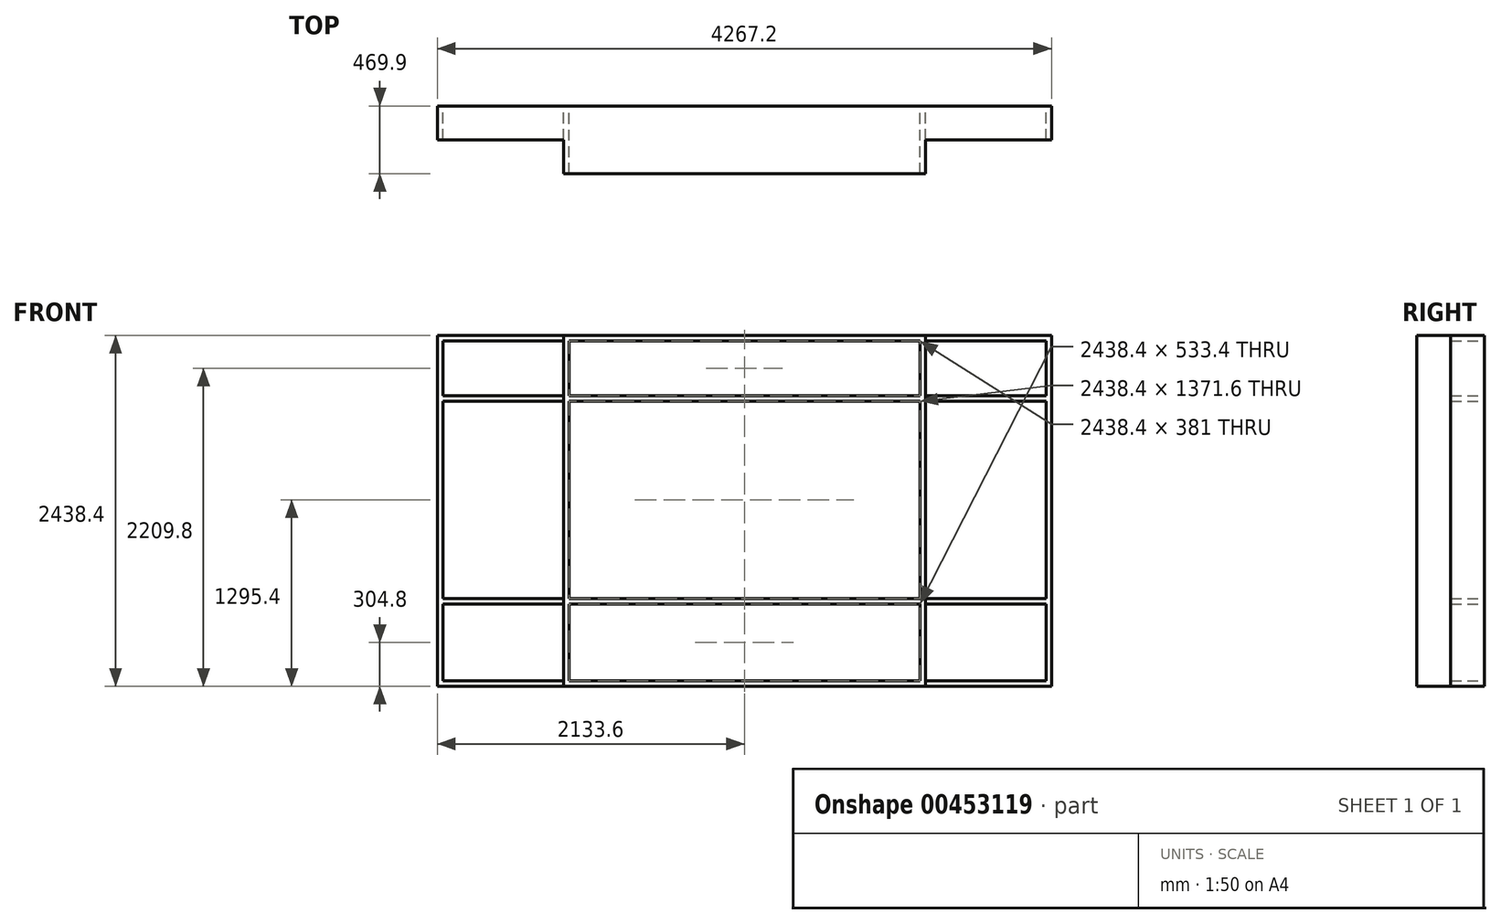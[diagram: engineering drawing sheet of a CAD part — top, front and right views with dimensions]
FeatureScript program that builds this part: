
annotation { "Feature Type Name" : "Feature", "Feature Type Description" : "" }
export const myFeature = defineFeature(function(context is Context, id is Id, definition is map)
    precondition{}
    {
        {
            var Q0;
            Q0=qCreatedBy(makeId("Front.planeOp"),FACE);
            var sketch = newSketch(context, id + "F0", { "sketchPlane" : qUnion([Q0])});
            skLineSegment(sketch, "E0.bottom", {"start": v(2133.6, 1219.2) * mm, "end": v(-2133.6, 1219.2) * mm});
            skLineSegment(sketch, "E0.top", {"start": v(2133.6, -1219.2) * mm, "end": v(457.2, -1219.2) * mm});
            skLineSegment(sketch, "E0.left", {"start": v(2133.6, 1219.2) * mm, "end": v(2133.6, -1219.2) * mm});
            skLineSegment(sketch, "E0.right", {"start": v(-2133.6, 1219.2) * mm, "end": v(-2133.6, -1219.2) * mm});
            skPoint(sketch, "E0.middle", {"position": v(0, 0) * mm});
            skLineSegment(sketch, "E1.0", {"start": v(2095.5, 762) * mm, "end": v(1257.3, 762) * mm});
            skLineSegment(sketch, "E2.0", {"start": v(-1219.2, 1181.1) * mm, "end": v(-1219.2, -1181.1) * mm});
            skLineSegment(sketch, "E3.0", {"start": v(1219.2, 1181.1) * mm, "end": v(1219.2, -1181.1) * mm});
            skLineSegment(sketch, "E4.0", {"start": v(2095.5, -609.6) * mm, "end": v(1257.3, -609.6) * mm});
            skPoint(sketch, "E5", {"position": v(-1219.2, -609.6) * mm});
            skPoint(sketch, "E6", {"position": v(1219.2, 762) * mm});
            skPoint(sketch, "E7", {"position": v(-1219.2, 762) * mm});
            skPoint(sketch, "E8", {"position": v(1219.2, -609.6) * mm});
            skLineSegment(sketch, "E9", {"start": v(457.2, -609.6) * mm, "end": v(-457.2, -609.6) * mm});
            skLineSegment(sketch, "E10", {"start": v(-457.2, -609.6) * mm, "end": v(-457.2, -609.6) * mm});
            skLineSegment(sketch, "E11", {"start": v(-457.2, -609.6) * mm, "end": v(-1219.2, -609.6) * mm});
            skLineSegment(sketch, "E12", {"start": v(-457.2, -1219.2) * mm, "end": v(-2133.6, -1219.2) * mm});
            skLineSegment(sketch, "E13", {"start": v(457.2, -1219.2) * mm, "end": v(-457.2, -1219.2) * mm});
            skLineSegment(sketch, "E14.0", {"start": v(-2095.5, 1181.1) * mm, "end": v(-2095.5, -1181.1) * mm});
            skLineSegment(sketch, "E15.0", {"start": v(-1257.3, 1181.1) * mm, "end": v(-1257.3, -1181.1) * mm});
            skLineSegment(sketch, "E16.0", {"start": v(2133.6, 1181.1) * mm, "end": v(-2133.6, 1181.1) * mm});
            skLineSegment(sketch, "E17.0", {"start": v(2095.5, 800.1) * mm, "end": v(1257.3, 800.1) * mm});
            skLineSegment(sketch, "E18.0", {"start": v(1257.3, 1181.1) * mm, "end": v(1257.3, -1181.1) * mm});
            skLineSegment(sketch, "E19.0", {"start": v(2095.5, 1181.1) * mm, "end": v(2095.5, -1181.1) * mm});
            skLineSegment(sketch, "E20.0", {"start": v(457.2, -647.7) * mm, "end": v(-457.2, -647.7) * mm});
            skLineSegment(sketch, "E21.0", {"start": v(2095.5, -647.7) * mm, "end": v(1257.3, -647.7) * mm});
            skLineSegment(sketch, "E22.0", {"start": v(-457.2, -647.7) * mm, "end": v(-1219.2, -647.7) * mm});
            skLineSegment(sketch, "E23.0", {"start": v(2133.6, -1181.1) * mm, "end": v(457.2, -1181.1) * mm});
            skLineSegment(sketch, "E24.0", {"start": v(457.2, -1181.1) * mm, "end": v(-457.2, -1181.1) * mm});
            skLineSegment(sketch, "E25.0", {"start": v(-457.2, -1181.1) * mm, "end": v(-2133.6, -1181.1) * mm});
            skLineSegment(sketch, "E26.trimOffspring", {"start": v(1219.2, -609.6) * mm, "end": v(457.2, -609.6) * mm});
            skLineSegment(sketch, "E27.trimOffspring", {"start": v(1219.2, -647.7) * mm, "end": v(457.2, -647.7) * mm});
            skLineSegment(sketch, "E28.trimOffspring", {"start": v(-1257.3, -609.6) * mm, "end": v(-2095.5, -609.6) * mm});
            skLineSegment(sketch, "E29.trimOffspring", {"start": v(-1257.3, -647.7) * mm, "end": v(-2095.5, -647.7) * mm});
            skLineSegment(sketch, "E30.trimOffspring", {"start": v(-1257.3, 800.1) * mm, "end": v(-2095.5, 800.1) * mm});
            skLineSegment(sketch, "E31.trimOffspring", {"start": v(-1257.3, 762) * mm, "end": v(-2095.5, 762) * mm});
            skLineSegment(sketch, "E32.trimOffspring", {"start": v(1219.2, 800.1) * mm, "end": v(-1219.2, 800.1) * mm});
            skLineSegment(sketch, "E33.trimOffspring", {"start": v(1219.2, 762) * mm, "end": v(-1219.2, 762) * mm});
            skLineSegment(sketch, "E34", {"start": v(1257.3, 1181.1) * mm, "end": v(1257.3, 1219.2) * mm});
            skLineSegment(sketch, "E35", {"start": v(-1257.3, 1181.1) * mm, "end": v(-1257.3, 1219.2) * mm});
            skLineSegment(sketch, "E36", {"start": v(1257.3, -1181.1) * mm, "end": v(1257.3, -1219.2) * mm});
            skLineSegment(sketch, "E37", {"start": v(-1257.3, -1181.1) * mm, "end": v(-1257.3, -1219.2) * mm});
            skSolve(sketch);
        }
        {
            var Q0;
            {var subQ3=sQuery(id+"F0.wireOp",EDGE,"E13");Q0=makeQuery(id+"F0.imprint","IMPRINT",FACE,{"disambiguationData":[TD([[makeQuery(id+"F0.imprint","IMPRINT",EDGE,{"derivedFrom":subQ3}),-1.0]])]});}
            var Q1;
            {var subQ5=sQuery(id+"F0.wireOp",EDGE,"E16.0");var subQ8=sQuery(id+"F0.wireOp",EDGE,"E3.0");var subQ11=makeQuery(id+"F0.imprint","INTERSECT",VERTEX,{"derivedFrom":[subQ8,subQ5]});Q1=makeQuery(id+"F0.imprint","IMPRINT",FACE,{"disambiguationData":[TD([[makeQuery(id+"F0.imprint","IMPRINT",EDGE,{"disambiguationData":[TD([[subQ11,-1.0]])],"derivedFrom":subQ8}),1.0]])]});}
            var Q2;
            Q2=makeQuery(id+"F0.imprint","IMPRINT",FACE,{"disambiguationData":[TD([[makeQuery(id+"F0.imprint","IMPRINT",EDGE,{"derivedFrom":sQuery(id+"F0.wireOp",EDGE,"E9")}),1.0]])]});
            var Q3;
            {var subQ0=sQuery(id+"F0.wireOp",EDGE,"E16.0");var subQ5=sQuery(id+"F0.wireOp",EDGE,"E2.0");var subQ9=makeQuery(id+"F0.imprint","INTERSECT",VERTEX,{"derivedFrom":[subQ5,subQ0]});Q3=makeQuery(id+"F0.imprint","IMPRINT",FACE,{"disambiguationData":[TD([[makeQuery(id+"F0.imprint","IMPRINT",EDGE,{"disambiguationData":[TD([[subQ9,-1.0]])],"derivedFrom":subQ5}),-1.0]])]});}
            var Q4;
            {var subQ4=sQuery(id+"F0.wireOp",EDGE,"E34");Q4=makeQuery(id+"F0.imprint","IMPRINT",FACE,{"disambiguationData":[TD([[makeQuery(id+"F0.imprint","IMPRINT",EDGE,{"derivedFrom":subQ4}),1.0]])]});}
            var Q5;
            {var subQ0=sQuery(id+"F0.wireOp",EDGE,"E32.trimOffspring");Q5=makeQuery(id+"F0.imprint","IMPRINT",FACE,{"disambiguationData":[TD([[makeQuery(id+"F0.imprint","IMPRINT",EDGE,{"derivedFrom":subQ0}),1.0]])]});}
            extrude(context, id + "F1", {"entities" : qUnion([Q0, Q1, Q2, Q3, Q4, Q5]), "depth" : 469.9 * mm});
        }
        {
            var Q0;
            {var subQ0=sQuery(id+"F0.wireOp",EDGE,"E34");Q0=makeQuery(id+"F0.imprint","IMPRINT",FACE,{"disambiguationData":[TD([[makeQuery(id+"F0.imprint","IMPRINT",EDGE,{"derivedFrom":subQ0}),-1.0]])]});}
            var Q1;
            {var subQ3=sQuery(id+"F0.wireOp",EDGE,"E16.0");var subQ4=sQuery(id+"F0.wireOp",EDGE,"E0.left");var subQ5=makeQuery(id+"F0.imprint","INTERSECT",VERTEX,{"derivedFrom":[subQ4,subQ3]});Q1=makeQuery(id+"F0.imprint","IMPRINT",FACE,{"disambiguationData":[TD([[makeQuery(id+"F0.imprint","IMPRINT",EDGE,{"disambiguationData":[TD([[subQ5,-1.0]])],"derivedFrom":subQ4}),-1.0]])]});}
            var Q2;
            {var subQ0=sQuery(id+"F0.wireOp",EDGE,"E1.0");Q2=makeQuery(id+"F0.imprint","IMPRINT",FACE,{"disambiguationData":[TD([[makeQuery(id+"F0.imprint","IMPRINT",EDGE,{"derivedFrom":subQ0}),-1.0]])]});}
            var Q3;
            {var subQ0=sQuery(id+"F0.wireOp",EDGE,"E4.0");Q3=makeQuery(id+"F0.imprint","IMPRINT",FACE,{"disambiguationData":[TD([[makeQuery(id+"F0.imprint","IMPRINT",EDGE,{"derivedFrom":subQ0}),1.0]])]});}
            var Q4;
            {var subQ0=sQuery(id+"F0.wireOp",EDGE,"E36");Q4=makeQuery(id+"F0.imprint","IMPRINT",FACE,{"disambiguationData":[TD([[makeQuery(id+"F0.imprint","IMPRINT",EDGE,{"derivedFrom":subQ0}),1.0]])]});}
            var Q5;
            {var subQ0=sQuery(id+"F0.wireOp",EDGE,"E28.trimOffspring");Q5=makeQuery(id+"F0.imprint","IMPRINT",FACE,{"disambiguationData":[TD([[makeQuery(id+"F0.imprint","IMPRINT",EDGE,{"derivedFrom":subQ0}),1.0]])]});}
            var Q6;
            {var subQ4=sQuery(id+"F0.wireOp",EDGE,"E37");Q6=makeQuery(id+"F0.imprint","IMPRINT",FACE,{"disambiguationData":[TD([[makeQuery(id+"F0.imprint","IMPRINT",EDGE,{"derivedFrom":subQ4}),-1.0]])]});}
            var Q7;
            {var subQ3=sQuery(id+"F0.wireOp",EDGE,"E16.0");var subQ6=sQuery(id+"F0.wireOp",EDGE,"E0.right");var subQ7=makeQuery(id+"F0.imprint","INTERSECT",VERTEX,{"derivedFrom":[subQ6,subQ3]});Q7=makeQuery(id+"F0.imprint","IMPRINT",FACE,{"disambiguationData":[TD([[makeQuery(id+"F0.imprint","IMPRINT",EDGE,{"disambiguationData":[TD([[subQ7,-1.0]])],"derivedFrom":subQ6}),1.0]])]});}
            var Q8;
            {var subQ0=sQuery(id+"F0.wireOp",EDGE,"E30.trimOffspring");Q8=makeQuery(id+"F0.imprint","IMPRINT",FACE,{"disambiguationData":[TD([[makeQuery(id+"F0.imprint","IMPRINT",EDGE,{"derivedFrom":subQ0}),1.0]])]});}
            var Q9;
            {var subQ4=sQuery(id+"F0.wireOp",EDGE,"E35");Q9=makeQuery(id+"F0.imprint","IMPRINT",FACE,{"disambiguationData":[TD([[makeQuery(id+"F0.imprint","IMPRINT",EDGE,{"derivedFrom":subQ4}),1.0]])]});}
            extrude(context, id + "F2", {"entities" : qUnion([Q0, Q1, Q2, Q3, Q4, Q5, Q6, Q7, Q8, Q9]), "operationType" : NewBodyOperationType.ADD, "depth" : 234.95 * mm});
        }
    });
